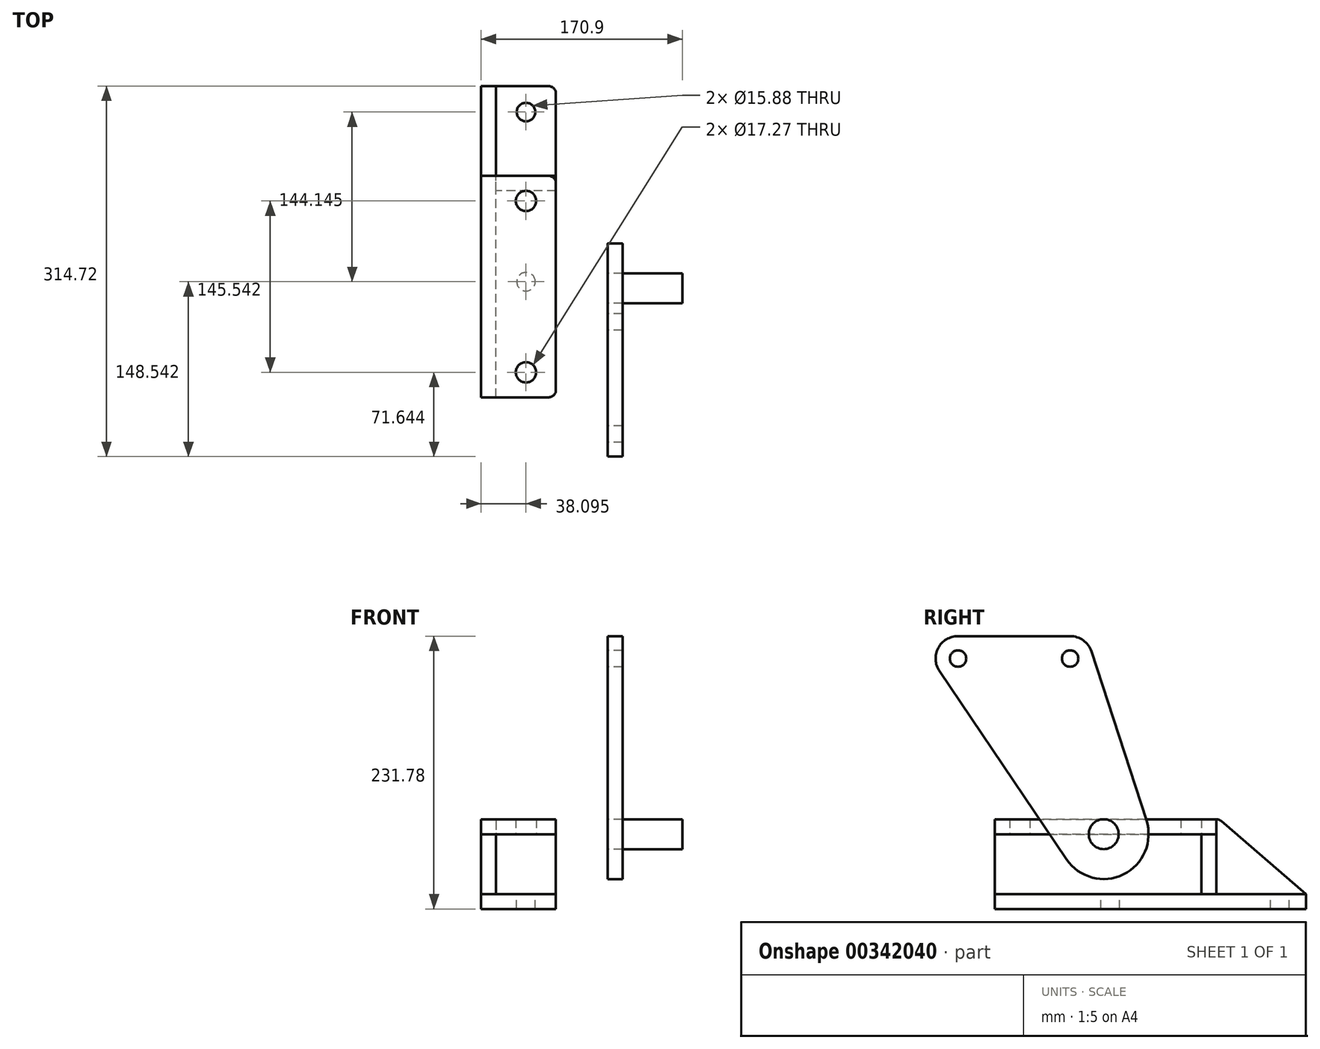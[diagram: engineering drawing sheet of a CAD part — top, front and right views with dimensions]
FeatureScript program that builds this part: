
annotation { "Feature Type Name" : "Feature", "Feature Type Description" : "" }
export const myFeature = defineFeature(function(context is Context, id is Id, definition is map)
    precondition{}
    {
        {
            var Q0;
            Q0=qCreatedBy(makeId("Right.planeOp"),FACE);
            var sketch = newSketch(context, id + "F0", { "sketchPlane" : qUnion([Q0])});
            skLineSegment(sketch, "E0", {"start": v(0, 0) * mm, "end": v(0, 149.23) * mm, "construction": true});
            skCircle(sketch, "E1", {"center": v(0, 0) * mm, "radius": 12.7 * mm});
            skCircle(sketch, "E2", {"center": v(-123.83, 149.23) * mm, "radius": 6.99 * mm});
            skCircle(sketch, "E3", {"center": v(-28.58, 149.23) * mm, "radius": 6.99 * mm});
            skLineSegment(sketch, "E4", {"start": v(-123.83, 149.23) * mm, "end": v(-28.58, 149.23) * mm, "construction": true});
            skArc(sketch, "E5", {"start": v(-123.83, 168.28) * mm, "mid": v(-140.65, 158.16) * mm, "end": v(-139.6, 138.56) * mm});
            skArc(sketch, "E6", {"start": v(-10.46, 155.13) * mm, "mid": v(-17.38, 164.64) * mm, "end": v(-28.58, 168.28) * mm});
            skArc(sketch, "E7", {"start": v(-31.57, -21.33) * mm, "mid": v(16.73, -34.23) * mm, "end": v(36.23, 11.8) * mm});
            skLineSegment(sketch, "E8", {"start": v(-10.46, 155.13) * mm, "end": v(36.23, 11.8) * mm});
            skLineSegment(sketch, "E9", {"start": v(-139.6, 138.56) * mm, "end": v(-31.57, -21.33) * mm});
            skLineSegment(sketch, "E10", {"start": v(-123.83, 168.28) * mm, "end": v(-28.58, 168.28) * mm});
            skSolve(sketch);
        }
        {
            var Q0;
            Q0=makeQuery(id+"F0.imprint","IMPRINT",FACE,{"disambiguationData":[TD([[makeQuery(id+"F0.imprint","IMPRINT",EDGE,{"derivedFrom":sQuery(id+"F0.wireOp",EDGE,"E1")}),1.0]])]});
            extrude(context, id + "F1", {"entities" : qUnion([Q0]), "depth" : 63.5 * mm});
        }
        {
            var Q0;
            Q0 = qSketchRegion(id + "F0", true);
            extrude(context, id + "F2", {"entities" : qUnion([Q0]), "depth" : 12.7 * mm});
        }
        {
            var Q0;
            Q0=qCreatedBy(makeId("Top.planeOp"),FACE);
            var sketch = newSketch(context, id + "F3", { "sketchPlane" : qUnion([Q0])});
            skLineSegment(sketch, "E11", {"start": v(-107.4, 95.64) * mm, "end": v(-50.25, 95.64) * mm});
            skLineSegment(sketch, "E12", {"start": v(-43.9, 89.3) * mm, "end": v(-43.9, -86.22) * mm});
            skLineSegment(sketch, "E13", {"start": v(-50.25, -92.57) * mm, "end": v(-107.4, -92.57) * mm});
            skLineSegment(sketch, "E14", {"start": v(-107.4, -92.57) * mm, "end": v(-107.4, 95.64) * mm});
            skLineSegment(sketch, "E15", {"start": v(-69.3, 95.64) * mm, "end": v(-69.3, -92.57) * mm, "construction": true});
            skCircle(sketch, "E16", {"center": v(-69.3, 74.3) * mm, "radius": 8.64 * mm});
            skCircle(sketch, "E17", {"center": v(-69.3, -71.24) * mm, "radius": 8.64 * mm});
            skPoint(sketch, "E18.visualSharp", {"position": v(-43.9, 95.64) * mm});
            skArc(sketch, "E18.filletArc", {"start": v(-43.9, 89.3) * mm, "mid": v(-45.76, 93.78) * mm, "end": v(-50.25, 95.64) * mm});
            skPoint(sketch, "E19.visualSharp", {"position": v(-43.9, -92.57) * mm});
            skArc(sketch, "E19.filletArc", {"start": v(-50.25, -92.57) * mm, "mid": v(-45.76, -90.71) * mm, "end": v(-43.9, -86.22) * mm});
            skSolve(sketch);
        }
        {
            var Q0;
            Q0 = qSketchRegion(id + "F3", true);
            extrude(context, id + "F4", {"entities" : qUnion([Q0]), "depth" : 12.7 * mm});
        }
        {
            var Q0;
            Q0=makeQuery(id+"F4.opExtrude","SWEPT_FACE",FACE,{"disambiguationData":[OSD([sQuery(id+"F3.wireOp",EDGE,"E14")])]});
            var sketch = newSketch(context, id + "F5", { "sketchPlane" : qUnion([Q0])});
            skLineSegment(sketch, "E20", {"start": v(-99.78, 11.16) * mm, "end": v(-171.84, -50.8) * mm});
            skArc(sketch, "E21", {"start": v(-95.64, 12.7) * mm, "mid": v(-97.85, 12.3) * mm, "end": v(-99.78, 11.16) * mm});
            skLineSegment(sketch, "E22", {"start": v(-95.64, 12.7) * mm, "end": v(-95.64, 0) * mm});
            skLineSegment(sketch, "E23", {"start": v(-95.64, 0) * mm, "end": v(92.57, 0) * mm});
            skLineSegment(sketch, "E24", {"start": v(92.57, 0) * mm, "end": v(92.57, -50.8) * mm});
            skLineSegment(sketch, "E25", {"start": v(92.57, -50.8) * mm, "end": v(-171.84, -50.8) * mm});
            skSolve(sketch);
        }
        {
            var Q0;
            Q0 = qSketchRegion(id + "F5", true);
            extrude(context, id + "F6", {"entities" : qUnion([Q0]), "oppositeDirection" : true, "depth" : 12.7 * mm});
        }
        {
            var Q0;
            Q0=makeQuery(id+"F6.opExtrude","CAP_FACE",FACE,{"disambiguationData":[OSD([sQuery(id+"F5.wireOp",EDGE,"E20"),sQuery(id+"F5.wireOp",EDGE,"E21"),sQuery(id+"F5.wireOp",EDGE,"E22"),sQuery(id+"F5.wireOp",EDGE,"E23"),sQuery(id+"F5.wireOp",EDGE,"E24"),sQuery(id+"F5.wireOp",EDGE,"E25")])],"isStart":false});
            var sketch = newSketch(context, id + "F7", { "sketchPlane" : qUnion([Q0])});
            skLineSegment(sketch, "E26.bottom", {"start": v(82.94, 0) * mm, "end": v(95.64, 0) * mm});
            skLineSegment(sketch, "E26.top", {"start": v(82.94, -50.8) * mm, "end": v(95.64, -50.8) * mm});
            skLineSegment(sketch, "E26.left", {"start": v(95.64, 0) * mm, "end": v(95.64, -50.8) * mm});
            skLineSegment(sketch, "E26.right", {"start": v(82.94, 0) * mm, "end": v(82.94, -50.8) * mm});
            skSolve(sketch);
        }
        {
            var Q0;
            Q0 = qSketchRegion(id + "F7", true);
            var Q1;
            Q1=makeQuery(id+"F4.opExtrude","SWEPT_FACE",FACE,{"disambiguationData":[OSD([sQuery(id+"F3.wireOp",EDGE,"E12")])]});
            extrude(context, id + "F8", {"entities" : qUnion([Q0]), "endBound" : BoundingType.UP_TO_SURFACE, "endBoundEntityFace" : qUnion([Q1]), "depth" : 12.7 * mm});
        }
        {
            var Q0;
            Q0=makeQuery(id+"F6.opExtrude","SWEPT_FACE",FACE,{"disambiguationData":[OSD([sQuery(id+"F5.wireOp",EDGE,"E25")])]});
            var sketch = newSketch(context, id + "F9", { "sketchPlane" : qUnion([Q0])});
            skLineSegment(sketch, "E27.bottom", {"start": v(-107.4, -171.84) * mm, "end": v(-50.25, -171.84) * mm});
            skLineSegment(sketch, "E27.top", {"start": v(-107.4, 92.57) * mm, "end": v(-50.25, 92.57) * mm});
            skLineSegment(sketch, "E27.left", {"start": v(-107.4, -171.84) * mm, "end": v(-107.4, 92.57) * mm});
            skLineSegment(sketch, "E27.right", {"start": v(-43.9, -165.5) * mm, "end": v(-43.9, 86.22) * mm});
            skLineSegment(sketch, "E28", {"start": v(-69.3, 92.57) * mm, "end": v(-69.3, -171.84) * mm, "construction": true});
            skLineSegment(sketch, "E29", {"start": v(-94.7, 92.57) * mm, "end": v(-50.25, 92.57) * mm, "construction": true});
            skPoint(sketch, "E30.visualSharp", {"position": v(-43.9, 92.57) * mm});
            skArc(sketch, "E30.filletArc", {"start": v(-43.9, 86.22) * mm, "mid": v(-45.76, 90.71) * mm, "end": v(-50.25, 92.57) * mm});
            skPoint(sketch, "E31.visualSharp", {"position": v(-43.9, -171.84) * mm});
            skArc(sketch, "E31.filletArc", {"start": v(-50.25, -171.84) * mm, "mid": v(-45.76, -169.98) * mm, "end": v(-43.9, -165.5) * mm});
            skCircle(sketch, "E32", {"center": v(-69.3, -5.66) * mm, "radius": 7.94 * mm});
            skCircle(sketch, "E33", {"center": v(-69.3, -149.8) * mm, "radius": 7.94 * mm});
            skSolve(sketch);
        }
        {
            var Q0;
            Q0 = qSketchRegion(id + "F9", true);
            extrude(context, id + "F10", {"entities" : qUnion([Q0]), "depth" : 12.7 * mm});
        }
    });
